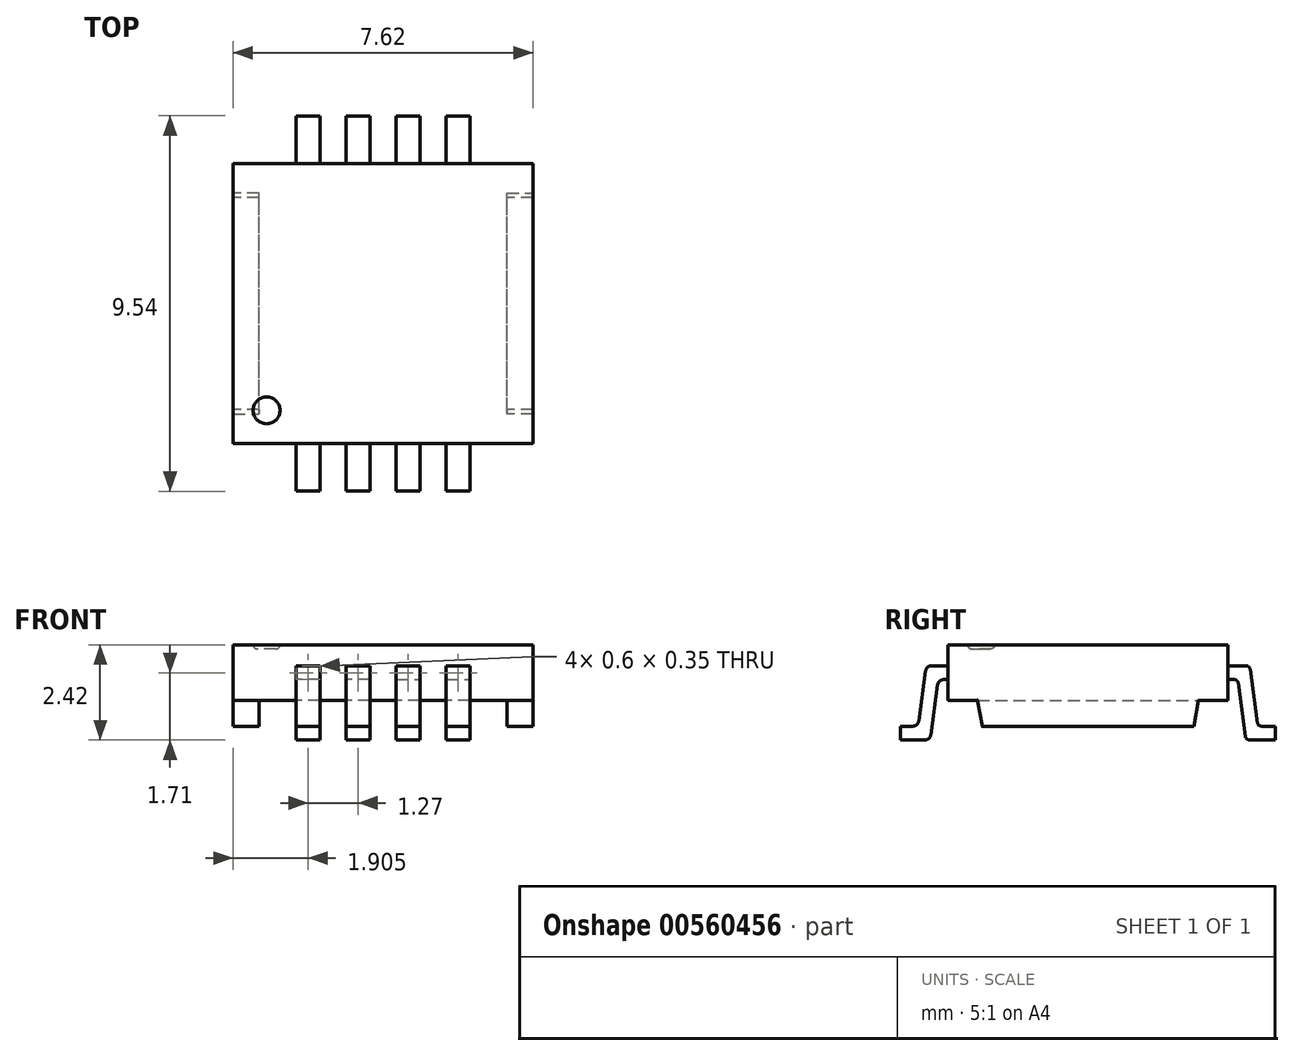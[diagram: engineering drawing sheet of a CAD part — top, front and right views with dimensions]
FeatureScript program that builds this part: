
annotation { "Feature Type Name" : "Feature", "Feature Type Description" : "" }
export const myFeature = defineFeature(function(context is Context, id is Id, definition is map)
    precondition{}
    {
        {
            var Q0;
            Q0=qCreatedBy(makeId("Top.planeOp"),FACE);
            var sketch = newSketch(context, id + "F0", { "sketchPlane" : qUnion([Q0])});
            skLineSegment(sketch, "E0.bottom", {"start": v(3.8, 3.56) * mm, "end": v(-3.81, 3.55) * mm});
            skLineSegment(sketch, "E0.top", {"start": v(3.81, -3.55) * mm, "end": v(-3.8, -3.56) * mm});
            skLineSegment(sketch, "E0.left", {"start": v(3.8, 3.56) * mm, "end": v(3.81, -3.56) * mm});
            skLineSegment(sketch, "E0.right", {"start": v(-3.81, 3.55) * mm, "end": v(-3.8, -3.56) * mm});
            skPoint(sketch, "E0.middle", {"position": v(0, 0) * mm});
            skSolve(sketch);
        }
        {
            var Q0;
            Q0=makeQuery(id+"F0.imprint","IMPRINT",FACE,{"disambiguationData":[TD([[makeQuery(id+"F0.imprint","IMPRINT",EDGE,{"derivedFrom":sQuery(id+"F0.wireOp",EDGE,"E0.bottom")}),1.0]])]});
            var Q1;
            Q1=makeQuery(id+"F0.imprint","IMPRINT",FACE,{"disambiguationData":[TD([[makeQuery(id+"F0.imprint","IMPRINT",EDGE,{"derivedFrom":sQuery(id+"F0.wireOp",EDGE,"f8ecaba3-d954-4120-b82d-af37b7497bcb0.MirrorCS")}),-1.0]])]});
            var Q2;
            Q2=makeQuery(id+"F0.imprint","IMPRINT",FACE,{"disambiguationData":[TD([[makeQuery(id+"F0.imprint","IMPRINT",EDGE,{"derivedFrom":sQuery(id+"F0.wireOp",EDGE,"WD66FqTf-apUJ-U9uG-5Enu-XqBL7MFoTnpj")}),-1.0]])]});
            extrude(context, id + "F1", {"entities" : qUnion([Q0, Q1, Q2]), "endBound" : BoundingType.SYMMETRIC, "depth" : 1.41 * mm, "offsetDistance" : 25 * mm});
        }
        {
            var Q0;
            Q0=makeQuery(id+"F1.opExtrude","CAP_FACE",FACE,{"disambiguationData":[OSD([sQuery(id+"F0.wireOp",EDGE,"E0.bottom"),sQuery(id+"F0.wireOp",EDGE,"E0.top"),sQuery(id+"F0.wireOp",EDGE,"E0.left"),sQuery(id+"F0.wireOp",EDGE,"E0.right")])],"isStart":true});
            var sketch = newSketch(context, id + "F2", { "sketchPlane" : qUnion([Q0])});
            skLineSegment(sketch, "E1", {"start": v(-3.8, 0) * mm, "end": v(-3.8, 2.81) * mm});
            skLineSegment(sketch, "E2", {"start": v(-3.8, 2.81) * mm, "end": v(-3.15, 2.81) * mm});
            skLineSegment(sketch, "E3", {"start": v(-3.15, 2.81) * mm, "end": v(-3.15, -2.81) * mm});
            skLineSegment(sketch, "E4", {"start": v(-3.15, -2.81) * mm, "end": v(-3.81, -2.81) * mm});
            skLineSegment(sketch, "E5", {"start": v(-3.8, -2.81) * mm, "end": v(-3.8, 0) * mm});
            skLineSegment(sketch, "E6.MirrorCS", {"start": v(3.8, 2.81) * mm, "end": v(3.15, 2.81) * mm});
            skLineSegment(sketch, "E7.MirrorCS", {"start": v(3.15, 2.81) * mm, "end": v(3.15, -2.81) * mm});
            skLineSegment(sketch, "E8.MirrorCS", {"start": v(3.8, 0) * mm, "end": v(3.8, 2.81) * mm});
            skLineSegment(sketch, "E9.MirrorCS", {"start": v(3.8, -2.81) * mm, "end": v(3.8, 0) * mm});
            skLineSegment(sketch, "E10.MirrorCS", {"start": v(3.15, -2.81) * mm, "end": v(3.81, -2.81) * mm});
            skSolve(sketch);
        }
        {
            var Q0;
            Q0=makeQuery(id+"F2.imprint","IMPRINT",FACE,{"disambiguationData":[TD([[makeQuery(id+"F2.imprint","IMPRINT",EDGE,{"derivedFrom":sQuery(id+"F2.wireOp",EDGE,"E1")}),-1.0]])]});
            var Q1;
            Q1=makeQuery(id+"F2.imprint","IMPRINT",FACE,{"disambiguationData":[TD([[makeQuery(id+"F2.imprint","IMPRINT",EDGE,{"derivedFrom":sQuery(id+"F2.wireOp",EDGE,"E6.MirrorCS")}),1.0]])]});
            extrude(context, id + "F3", {"entities" : qUnion([Q0, Q1]), "operationType" : NewBodyOperationType.ADD, "depth" : 0.66 * mm, "offsetDistance" : 25 * mm});
        }
        {
            var Q0;
            Q0=makeQuery(id+"F3.boolean.opBoolean","MERGE",FACE,{"derivedFrom":[makeQuery(id+"F1.opExtrude","SWEPT_FACE",FACE,{"disambiguationData":[OSD([sQuery(id+"F0.wireOp",EDGE,"E0.right")])]}),makeQuery(id+"F3.opExtrude","SWEPT_FACE",FACE,{"disambiguationData":[OSD([sQuery(id+"F2.wireOp",EDGE,"E1"),sQuery(id+"F2.wireOp",EDGE,"E5")])]})]});
            var sketch = newSketch(context, id + "F4", { "sketchPlane" : qUnion([Q0])});
            skLineSegment(sketch, "E11", {"start": v(2.8, -0.7) * mm, "end": v(2.69, -1.36) * mm});
            skLineSegment(sketch, "E12", {"start": v(2.69, -1.36) * mm, "end": v(2.8, -1.36) * mm});
            skLineSegment(sketch, "E13", {"start": v(2.8, -1.36) * mm, "end": v(2.8, -0.7) * mm});
            skLineSegment(sketch, "E14.MirrorCS", {"start": v(-2.81, -0.7) * mm, "end": v(-2.69, -1.36) * mm});
            skLineSegment(sketch, "E15.MirrorCS", {"start": v(-2.69, -1.36) * mm, "end": v(-2.81, -1.36) * mm});
            skLineSegment(sketch, "E16.MirrorCS", {"start": v(-2.81, -1.36) * mm, "end": v(-2.81, -0.7) * mm});
            skSolve(sketch);
        }
        {
            var Q0;
            Q0=makeQuery(id+"F4.imprint","IMPRINT",FACE,{"disambiguationData":[TD([[makeQuery(id+"F4.imprint","IMPRINT",EDGE,{"derivedFrom":sQuery(id+"F4.wireOp",EDGE,"E14.MirrorCS")}),-1.0]])]});
            var Q1;
            Q1=makeQuery(id+"F4.imprint","IMPRINT",FACE,{"disambiguationData":[TD([[makeQuery(id+"F4.imprint","IMPRINT",EDGE,{"derivedFrom":sQuery(id+"F4.wireOp",EDGE,"E11")}),1.0]])]});
            extrude(context, id + "F5", {"entities" : qUnion([Q0, Q1]), "operationType" : NewBodyOperationType.REMOVE, "oppositeDirection" : true, "depth" : 25 * mm, "offsetDistance" : 25 * mm});
        }
        {
            var Q0;
            Q0=makeQuery(id+"F1.opExtrude","CAP_EDGE",EDGE,{"disambiguationData":[OSD([sQuery(id+"F0.wireOp",EDGE,"E0.right")])],"isStart":false});
            var Q1;
            Q1=makeQuery(id+"F1.opExtrude","SWEPT_EDGE",EDGE,{"disambiguationData":[OSD([sQuery(id+"F0.wireOp",EDGE,"E0.top"),sQuery(id+"F0.wireOp",EDGE,"E0.right")])]});
            var Q2;
            Q2=makeQuery(id+"F1.opExtrude","CAP_EDGE",EDGE,{"disambiguationData":[OSD([sQuery(id+"F0.wireOp",EDGE,"E0.top")])],"isStart":false});
            var Q3;
            Q3=makeQuery(id+"F1.opExtrude","SWEPT_EDGE",EDGE,{"disambiguationData":[OSD([sQuery(id+"F0.wireOp",EDGE,"E0.bottom"),sQuery(id+"F0.wireOp",EDGE,"E0.right")])]});
            var Q4;
            Q4=makeQuery(id+"F1.opExtrude","SWEPT_EDGE",EDGE,{"disambiguationData":[OSD([sQuery(id+"F0.wireOp",EDGE,"E0.top"),sQuery(id+"F0.wireOp",EDGE,"E0.left")])]});
            var Q5;
            Q5=makeQuery(id+"F1.opExtrude","CAP_EDGE",EDGE,{"disambiguationData":[OSD([sQuery(id+"F0.wireOp",EDGE,"E0.left")])],"isStart":false});
            var Q6;
            Q6=makeQuery(id+"F1.opExtrude","SWEPT_EDGE",EDGE,{"disambiguationData":[OSD([sQuery(id+"F0.wireOp",EDGE,"E0.bottom"),sQuery(id+"F0.wireOp",EDGE,"E0.left")])]});
            var Q7;
            Q7=makeQuery(id+"F1.opExtrude","CAP_EDGE",EDGE,{"disambiguationData":[OSD([sQuery(id+"F0.wireOp",EDGE,"E0.bottom")])],"isStart":false});
            var Q8;
            Q8=makeQuery(id+"F1.opExtrude","CAP_EDGE",EDGE,{"disambiguationData":[OSD([sQuery(id+"F0.wireOp",EDGE,"E0.bottom")])],"isStart":true});
            var Q9;
            Q9=makeQuery(id+"F1.opExtrude","CAP_EDGE",EDGE,{"disambiguationData":[OSD([sQuery(id+"F0.wireOp",EDGE,"E0.top")])],"isStart":true});
            var Q10;
            {var subQ0=sQuery(id+"F0.wireOp",EDGE,"E0.left");var subQ1=sQuery(id+"F0.wireOp",EDGE,"E0.top");Q10=makeQuery(id+"F3.boolean.opBoolean","SPLIT",EDGE,{"disambiguationData":[TD([makeQuery(id+"F1.opExtrude","SWEPT_FACE",FACE,{"disambiguationData":[OSD([subQ1])]})])],"derivedFrom":makeQuery(id+"F1.opExtrude","CAP_EDGE",EDGE,{"disambiguationData":[OSD([subQ0])],"isStart":true})});}
            var Q11;
            Q11=makeQuery(id+"F5.boolean.opBoolean","INTERSECT",EDGE,{"derivedFrom":[makeQuery(id+"F3.boolean.opBoolean","MERGE",FACE,{"derivedFrom":[makeQuery(id+"F1.opExtrude","SWEPT_FACE",FACE,{"disambiguationData":[OSD([sQuery(id+"F0.wireOp",EDGE,"E0.left")])]}),makeQuery(id+"F3.opExtrude","SWEPT_FACE",FACE,{"disambiguationData":[OSD([sQuery(id+"F2.wireOp",EDGE,"E8.MirrorCS"),sQuery(id+"F2.wireOp",EDGE,"E9.MirrorCS")])]})]}),makeQuery(id+"F5.opExtrude","SWEPT_FACE",FACE,{"disambiguationData":[OSD([sQuery(id+"F4.wireOp",EDGE,"E11")])]})]});
            var Q12;
            Q12=makeQuery(id+"F5.boolean.opBoolean","INTERSECT",EDGE,{"derivedFrom":[makeQuery(id+"F3.boolean.opBoolean","MERGE",FACE,{"derivedFrom":[makeQuery(id+"F1.opExtrude","SWEPT_FACE",FACE,{"disambiguationData":[OSD([sQuery(id+"F0.wireOp",EDGE,"E0.left")])]}),makeQuery(id+"F3.opExtrude","SWEPT_FACE",FACE,{"disambiguationData":[OSD([sQuery(id+"F2.wireOp",EDGE,"E8.MirrorCS"),sQuery(id+"F2.wireOp",EDGE,"E9.MirrorCS")])]})]}),makeQuery(id+"F5.opExtrude","SWEPT_FACE",FACE,{"disambiguationData":[OSD([sQuery(id+"F4.wireOp",EDGE,"E14.MirrorCS")])]})]});
            var Q13;
            {var subQ0=sQuery(id+"F0.wireOp",EDGE,"E0.bottom");var subQ1=sQuery(id+"F0.wireOp",EDGE,"E0.left");Q13=makeQuery(id+"F3.boolean.opBoolean","SPLIT",EDGE,{"disambiguationData":[TD([makeQuery(id+"F1.opExtrude","SWEPT_FACE",FACE,{"disambiguationData":[OSD([subQ0])]})])],"derivedFrom":makeQuery(id+"F1.opExtrude","CAP_EDGE",EDGE,{"disambiguationData":[OSD([subQ1])],"isStart":true})});}
            var Q14;
            Q14=makeQuery(id+"F5.boolean.opBoolean","COPY",EDGE,{"derivedFrom":makeQuery(id+"F5.opExtrude","CAP_EDGE",EDGE,{"disambiguationData":[OSD([sQuery(id+"F4.wireOp",EDGE,"E11")])],"isStart":true})});
            var Q15;
            {var subQ0=sQuery(id+"F0.wireOp",EDGE,"E0.top");var subQ1=sQuery(id+"F0.wireOp",EDGE,"E0.right");Q15=makeQuery(id+"F3.boolean.opBoolean","SPLIT",EDGE,{"disambiguationData":[TD([makeQuery(id+"F1.opExtrude","SWEPT_FACE",FACE,{"disambiguationData":[OSD([subQ0])]})])],"derivedFrom":makeQuery(id+"F1.opExtrude","CAP_EDGE",EDGE,{"disambiguationData":[OSD([subQ1])],"isStart":true})});}
            var Q16;
            {var subQ0=sQuery(id+"F0.wireOp",EDGE,"E0.right");var subQ1=sQuery(id+"F0.wireOp",EDGE,"E0.bottom");Q16=makeQuery(id+"F3.boolean.opBoolean","SPLIT",EDGE,{"disambiguationData":[TD([makeQuery(id+"F1.opExtrude","SWEPT_FACE",FACE,{"disambiguationData":[OSD([subQ1])]})])],"derivedFrom":makeQuery(id+"F1.opExtrude","CAP_EDGE",EDGE,{"disambiguationData":[OSD([subQ0])],"isStart":true})});}
            var Q17;
            Q17=makeQuery(id+"F5.boolean.opBoolean","COPY",EDGE,{"derivedFrom":makeQuery(id+"F5.opExtrude","CAP_EDGE",EDGE,{"disambiguationData":[OSD([sQuery(id+"F4.wireOp",EDGE,"E14.MirrorCS")])],"isStart":true})});
            fillet(context, id + "F6", {"entities" : qUnion([Q0, Q1, Q2, Q3, Q4, Q5, Q6, Q7, Q8, Q9, Q10, Q11, Q12, Q13, Q14, Q15, Q16, Q17]), "radius" : 0.01 * mm, "tangentPropagation" : true, "allowEdgeOverflow" : false});
        }
        {
            var Q0;
            Q0=makeQuery(id+"F1.opExtrude","CAP_FACE",FACE,{"disambiguationData":[OSD([sQuery(id+"F0.wireOp",EDGE,"E0.bottom"),sQuery(id+"F0.wireOp",EDGE,"E0.top"),sQuery(id+"F0.wireOp",EDGE,"E0.left"),sQuery(id+"F0.wireOp",EDGE,"E0.right")])],"isStart":false});
            var sketch = newSketch(context, id + "F7", { "sketchPlane" : qUnion([Q0])});
            skCircle(sketch, "E17", {"center": v(-2.96, -2.71) * mm, "radius": 0.34 * mm});
            skSolve(sketch);
        }
        {
            var Q0;
            Q0=makeQuery(id+"F7.imprint","IMPRINT",FACE,{"disambiguationData":[TD([[makeQuery(id+"F7.imprint","IMPRINT",EDGE,{"derivedFrom":sQuery(id+"F7.wireOp",EDGE,"E17")}),1.0]])]});
            extrude(context, id + "F8", {"entities" : qUnion([Q0]), "operationType" : NewBodyOperationType.REMOVE, "oppositeDirection" : true, "depth" : 0.1 * mm, "offsetDistance" : 25 * mm});
        }
        {
            var Q0;
            Q0=makeQuery(id+"F8.boolean.opBoolean","COPY",EDGE,{"derivedFrom":makeQuery(id+"F8.opExtrude","CAP_EDGE",EDGE,{"disambiguationData":[OSD([sQuery(id+"F7.wireOp",EDGE,"E17")])],"isStart":false})});
            fillet(context, id + "F9", {"entities" : qUnion([Q0]), "radius" : 0.1 * mm, "tangentPropagation" : true, "allowEdgeOverflow" : false});
        }
        {
            var Q0;
            Q0=qCreatedBy(makeId("Right.planeOp"),FACE);
            var sketch = newSketch(context, id + "F10", { "sketchPlane" : qUnion([Q0])});
            skLineSegment(sketch, "E18", {"start": v(3.56, 0) * mm, "end": v(3.96, 0) * mm});
            skLineSegment(sketch, "E19", {"start": v(3.96, 0) * mm, "end": v(4.17, -1.53) * mm});
            skLineSegment(sketch, "E20", {"start": v(4.17, -1.53) * mm, "end": v(4.77, -1.53) * mm});
            skLineSegment(sketch, "E21.MirrorCS", {"start": v(-3.56, 0) * mm, "end": v(-3.96, 0) * mm});
            skLineSegment(sketch, "E22.MirrorCS", {"start": v(-3.96, 0) * mm, "end": v(-4.17, -1.53) * mm});
            skLineSegment(sketch, "E23.MirrorCS", {"start": v(-4.17, -1.53) * mm, "end": v(-4.77, -1.53) * mm});
            skSolve(sketch);
        }
        {
            var Q0;
            Q0=makeQuery(id+"F1.opExtrude","SWEPT_FACE",FACE,{"disambiguationData":[OSD([sQuery(id+"F0.wireOp",EDGE,"E0.bottom")])]});
            var sketch = newSketch(context, id + "F11", { "sketchPlane" : qUnion([Q0])});
            skLineSegment(sketch, "E24.bottom", {"start": v(-0.34, -0.17) * mm, "end": v(-0.94, -0.17) * mm});
            skLineSegment(sketch, "E24.top", {"start": v(-0.34, 0.18) * mm, "end": v(-0.94, 0.18) * mm});
            skLineSegment(sketch, "E24.left", {"start": v(-0.34, -0.17) * mm, "end": v(-0.34, 0.18) * mm});
            skLineSegment(sketch, "E24.right", {"start": v(-0.94, -0.18) * mm, "end": v(-0.94, 0.17) * mm});
            skPoint(sketch, "E24.middle", {"position": v(-0.64, 0) * mm});
            skLineSegment(sketch, "E25.bottom", {"start": v(0.33, -0.17) * mm, "end": v(0.93, -0.17) * mm});
            skLineSegment(sketch, "E25.top", {"start": v(0.33, 0.17) * mm, "end": v(0.93, 0.17) * mm});
            skLineSegment(sketch, "E25.left", {"start": v(0.33, -0.17) * mm, "end": v(0.33, 0.18) * mm});
            skLineSegment(sketch, "E25.right", {"start": v(0.93, -0.17) * mm, "end": v(0.93, 0.18) * mm});
            skPoint(sketch, "E25.middle", {"position": v(0.63, 0) * mm});
            skLineSegment(sketch, "E26.bottom", {"start": v(1.6, 0.17) * mm, "end": v(2.2, 0.17) * mm});
            skLineSegment(sketch, "E26.top", {"start": v(1.6, -0.17) * mm, "end": v(2.2, -0.17) * mm});
            skLineSegment(sketch, "E26.left", {"start": v(1.6, 0.17) * mm, "end": v(1.6, -0.17) * mm});
            skLineSegment(sketch, "E26.right", {"start": v(2.2, 0.17) * mm, "end": v(2.2, -0.17) * mm});
            skPoint(sketch, "E26.middle", {"position": v(1.9, 0) * mm});
            skLineSegment(sketch, "E27.MirrorCS", {"start": v(-1.6, 0.17) * mm, "end": v(-1.6, -0.17) * mm});
            skLineSegment(sketch, "E28.MirrorCS", {"start": v(-1.6, 0.17) * mm, "end": v(-2.2, 0.17) * mm});
            skLineSegment(sketch, "E29.MirrorCS", {"start": v(-2.2, 0.17) * mm, "end": v(-2.2, -0.17) * mm});
            skLineSegment(sketch, "E30.MirrorCS", {"start": v(-1.6, -0.17) * mm, "end": v(-2.2, -0.17) * mm});
            skSolve(sketch);
        }
        {
            var Q0;
            Q0=makeQuery(id+"F11.imprint","IMPRINT",FACE,{"disambiguationData":[TD([[makeQuery(id+"F11.imprint","IMPRINT",EDGE,{"derivedFrom":sQuery(id+"F11.wireOp",EDGE,"E27.MirrorCS")}),-1.0]])]});
            var Q1;
            Q1=makeQuery(id+"F11.imprint","IMPRINT",FACE,{"disambiguationData":[TD([[makeQuery(id+"F11.imprint","IMPRINT",EDGE,{"derivedFrom":sQuery(id+"F11.wireOp",EDGE,"E24.bottom")}),-1.0]])]});
            var Q2;
            Q2=makeQuery(id+"F11.imprint","IMPRINT",FACE,{"disambiguationData":[TD([[makeQuery(id+"F11.imprint","IMPRINT",EDGE,{"derivedFrom":sQuery(id+"F11.wireOp",EDGE,"E25.bottom")}),1.0]])]});
            var Q3;
            Q3=makeQuery(id+"F11.imprint","IMPRINT",FACE,{"disambiguationData":[TD([[makeQuery(id+"F11.imprint","IMPRINT",EDGE,{"derivedFrom":sQuery(id+"F11.wireOp",EDGE,"E26.bottom")}),-1.0]])]});
            var Q4;
            Q4=sQuery(id+"F10.wireOp",EDGE,"E18");
            var Q5;
            Q5=sQuery(id+"F10.wireOp",EDGE,"E19");
            var Q6;
            Q6=sQuery(id+"F10.wireOp",EDGE,"E20");
            sweep(context, id + "F12", {"operationType" : NewBodyOperationType.ADD, "profiles" : qUnion([Q0, Q1, Q2, Q3]), "path" : qUnion([Q4, Q5, Q6])});
        }
        {
            var Q0;
            Q0=makeQuery(id+"F12.opSweep","MID_CAP_EDGE",EDGE,{"disambiguationData":[OSD([sQuery(id+"F10.wireOp",VERTEX,"E19.start"),sQuery(id+"F11.wireOp",EDGE,"E26.bottom")])],"capPos":1.0});
            var Q1;
            Q1=makeQuery(id+"F12.opSweep","MID_CAP_EDGE",EDGE,{"disambiguationData":[OSD([sQuery(id+"F10.wireOp",VERTEX,"E20.start"),sQuery(id+"F11.wireOp",EDGE,"E26.bottom")])],"capPos":2.0});
            var Q2;
            Q2=makeQuery(id+"F12.opSweep","MID_CAP_EDGE",EDGE,{"disambiguationData":[OSD([sQuery(id+"F10.wireOp",VERTEX,"E19.start"),sQuery(id+"F11.wireOp",EDGE,"E25.top")])],"capPos":1.0});
            var Q3;
            Q3=makeQuery(id+"F12.opSweep","MID_CAP_EDGE",EDGE,{"disambiguationData":[OSD([sQuery(id+"F10.wireOp",VERTEX,"E20.start"),sQuery(id+"F11.wireOp",EDGE,"E25.top")])],"capPos":2.0});
            var Q4;
            Q4=makeQuery(id+"F12.opSweep","MID_CAP_EDGE",EDGE,{"disambiguationData":[OSD([sQuery(id+"F10.wireOp",VERTEX,"E19.start"),sQuery(id+"F11.wireOp",EDGE,"E24.top")])],"capPos":1.0});
            var Q5;
            Q5=makeQuery(id+"F12.opSweep","MID_CAP_EDGE",EDGE,{"disambiguationData":[OSD([sQuery(id+"F10.wireOp",VERTEX,"E20.start"),sQuery(id+"F11.wireOp",EDGE,"E24.top")])],"capPos":2.0});
            var Q6;
            Q6=makeQuery(id+"F12.opSweep","MID_CAP_EDGE",EDGE,{"disambiguationData":[OSD([sQuery(id+"F10.wireOp",VERTEX,"E19.start"),sQuery(id+"F11.wireOp",EDGE,"E28.MirrorCS")])],"capPos":1.0});
            var Q7;
            Q7=makeQuery(id+"F12.opSweep","MID_CAP_EDGE",EDGE,{"disambiguationData":[OSD([sQuery(id+"F10.wireOp",VERTEX,"E20.start"),sQuery(id+"F11.wireOp",EDGE,"E28.MirrorCS")])],"capPos":2.0});
            var Q8;
            Q8=makeQuery(id+"F12.opSweep","MID_CAP_EDGE",EDGE,{"disambiguationData":[OSD([sQuery(id+"F10.wireOp",VERTEX,"E19.start"),sQuery(id+"F11.wireOp",EDGE,"E30.MirrorCS")])],"capPos":1.0});
            var Q9;
            Q9=makeQuery(id+"F12.opSweep","MID_CAP_EDGE",EDGE,{"disambiguationData":[OSD([sQuery(id+"F10.wireOp",VERTEX,"E19.start"),sQuery(id+"F11.wireOp",EDGE,"E24.bottom")])],"capPos":1.0});
            var Q10;
            Q10=makeQuery(id+"F12.opSweep","MID_CAP_EDGE",EDGE,{"disambiguationData":[OSD([sQuery(id+"F10.wireOp",VERTEX,"E19.start"),sQuery(id+"F11.wireOp",EDGE,"E25.bottom")])],"capPos":1.0});
            var Q11;
            Q11=makeQuery(id+"F12.opSweep","MID_CAP_EDGE",EDGE,{"disambiguationData":[OSD([sQuery(id+"F10.wireOp",VERTEX,"E19.start"),sQuery(id+"F11.wireOp",EDGE,"E26.top")])],"capPos":1.0});
            var Q12;
            Q12=makeQuery(id+"F12.opSweep","MID_CAP_EDGE",EDGE,{"disambiguationData":[OSD([sQuery(id+"F10.wireOp",VERTEX,"E20.start"),sQuery(id+"F11.wireOp",EDGE,"E26.top")])],"capPos":2.0});
            var Q13;
            Q13=makeQuery(id+"F12.opSweep","MID_CAP_EDGE",EDGE,{"disambiguationData":[OSD([sQuery(id+"F10.wireOp",VERTEX,"E20.start"),sQuery(id+"F11.wireOp",EDGE,"E25.bottom")])],"capPos":2.0});
            var Q14;
            Q14=makeQuery(id+"F12.opSweep","MID_CAP_EDGE",EDGE,{"disambiguationData":[OSD([sQuery(id+"F10.wireOp",VERTEX,"E20.start"),sQuery(id+"F11.wireOp",EDGE,"E24.bottom")])],"capPos":2.0});
            var Q15;
            Q15=makeQuery(id+"F12.opSweep","MID_CAP_EDGE",EDGE,{"disambiguationData":[OSD([sQuery(id+"F10.wireOp",VERTEX,"E20.start"),sQuery(id+"F11.wireOp",EDGE,"E30.MirrorCS")])],"capPos":2.0});
            fillet(context, id + "F13", {"entities" : qUnion([Q0, Q1, Q2, Q3, Q4, Q5, Q6, Q7, Q8, Q9, Q10, Q11, Q12, Q13, Q14, Q15]), "radius" : 0.1 * mm, "tangentPropagation" : true, "allowEdgeOverflow" : false});
        }
        {
            var Q0;
            Q0=makeQuery(id+"F1.opExtrude","SWEPT_FACE",FACE,{"disambiguationData":[OSD([sQuery(id+"F0.wireOp",EDGE,"E0.top")])]});
            var sketch = newSketch(context, id + "F14", { "sketchPlane" : qUnion([Q0])});
            skLineSegment(sketch, "E31.bottom", {"start": v(-1.6, 0.18) * mm, "end": v(-2.2, 0.18) * mm});
            skLineSegment(sketch, "E31.top", {"start": v(-1.6, -0.18) * mm, "end": v(-2.2, -0.18) * mm});
            skLineSegment(sketch, "E31.left", {"start": v(-1.6, 0.18) * mm, "end": v(-1.6, -0.18) * mm});
            skLineSegment(sketch, "E31.right", {"start": v(-2.2, 0.18) * mm, "end": v(-2.2, -0.18) * mm});
            skPoint(sketch, "E31.middle", {"position": v(-1.9, 0) * mm});
            skLineSegment(sketch, "E32.bottom", {"start": v(-0.34, 0.18) * mm, "end": v(-0.94, 0.18) * mm});
            skLineSegment(sketch, "E32.top", {"start": v(-0.34, -0.18) * mm, "end": v(-0.94, -0.18) * mm});
            skLineSegment(sketch, "E32.left", {"start": v(-0.34, 0.18) * mm, "end": v(-0.34, -0.18) * mm});
            skLineSegment(sketch, "E32.right", {"start": v(-0.94, 0.18) * mm, "end": v(-0.94, -0.18) * mm});
            skPoint(sketch, "E32.middle", {"position": v(-0.64, 0) * mm});
            skLineSegment(sketch, "E33.MirrorCS", {"start": v(0.33, 0.18) * mm, "end": v(0.33, -0.18) * mm});
            skLineSegment(sketch, "E34.MirrorCS", {"start": v(0.33, 0.18) * mm, "end": v(0.93, 0.18) * mm});
            skLineSegment(sketch, "E35.MirrorCS", {"start": v(0.33, -0.18) * mm, "end": v(0.93, -0.18) * mm});
            skLineSegment(sketch, "E36.MirrorCS", {"start": v(0.93, 0.18) * mm, "end": v(0.93, -0.18) * mm});
            skLineSegment(sketch, "E37.MirrorCS", {"start": v(1.6, 0.18) * mm, "end": v(1.6, -0.18) * mm});
            skLineSegment(sketch, "E38.MirrorCS", {"start": v(1.6, 0.18) * mm, "end": v(2.2, 0.18) * mm});
            skLineSegment(sketch, "E39.MirrorCS", {"start": v(2.2, 0.18) * mm, "end": v(2.2, -0.18) * mm});
            skLineSegment(sketch, "E40.MirrorCS", {"start": v(1.6, -0.18) * mm, "end": v(2.2, -0.18) * mm});
            skSolve(sketch);
        }
        {
            var Q0;
            Q0=makeQuery(id+"F14.imprint","IMPRINT",FACE,{"disambiguationData":[TD([[makeQuery(id+"F14.imprint","IMPRINT",EDGE,{"derivedFrom":sQuery(id+"F14.wireOp",EDGE,"E31.bottom")}),1.0]])]});
            var Q1;
            Q1=makeQuery(id+"F14.imprint","IMPRINT",FACE,{"disambiguationData":[TD([[makeQuery(id+"F14.imprint","IMPRINT",EDGE,{"derivedFrom":sQuery(id+"F14.wireOp",EDGE,"E32.bottom")}),1.0]])]});
            var Q2;
            Q2=makeQuery(id+"F14.imprint","IMPRINT",FACE,{"disambiguationData":[TD([[makeQuery(id+"F14.imprint","IMPRINT",EDGE,{"derivedFrom":sQuery(id+"F14.wireOp",EDGE,"E33.MirrorCS")}),1.0]])]});
            var Q3;
            Q3=makeQuery(id+"F14.imprint","IMPRINT",FACE,{"disambiguationData":[TD([[makeQuery(id+"F14.imprint","IMPRINT",EDGE,{"derivedFrom":sQuery(id+"F14.wireOp",EDGE,"E37.MirrorCS")}),1.0]])]});
            var Q4;
            Q4=sQuery(id+"F10.wireOp",EDGE,"E21.MirrorCS");
            var Q5;
            Q5=sQuery(id+"F10.wireOp",EDGE,"E22.MirrorCS");
            var Q6;
            Q6=sQuery(id+"F10.wireOp",EDGE,"E23.MirrorCS");
            sweep(context, id + "F15", {"operationType" : NewBodyOperationType.ADD, "profiles" : qUnion([Q0, Q1, Q2, Q3]), "path" : qUnion([Q4, Q5, Q6])});
        }
        {
            var Q0;
            Q0=makeQuery(id+"F15.opSweep","MID_CAP_EDGE",EDGE,{"disambiguationData":[OSD([sQuery(id+"F10.wireOp",VERTEX,"E22.MirrorCS.start"),sQuery(id+"F14.wireOp",EDGE,"E31.bottom")])],"capPos":1.0});
            var Q1;
            Q1=makeQuery(id+"F15.opSweep","MID_CAP_EDGE",EDGE,{"disambiguationData":[OSD([sQuery(id+"F10.wireOp",VERTEX,"E22.MirrorCS.start"),sQuery(id+"F14.wireOp",EDGE,"E32.bottom")])],"capPos":1.0});
            var Q2;
            Q2=makeQuery(id+"F15.opSweep","MID_CAP_EDGE",EDGE,{"disambiguationData":[OSD([sQuery(id+"F10.wireOp",VERTEX,"E22.MirrorCS.start"),sQuery(id+"F14.wireOp",EDGE,"E34.MirrorCS")])],"capPos":1.0});
            var Q3;
            Q3=makeQuery(id+"F15.opSweep","MID_CAP_EDGE",EDGE,{"disambiguationData":[OSD([sQuery(id+"F10.wireOp",VERTEX,"E22.MirrorCS.start"),sQuery(id+"F14.wireOp",EDGE,"E38.MirrorCS")])],"capPos":1.0});
            var Q4;
            Q4=makeQuery(id+"F15.opSweep","MID_CAP_EDGE",EDGE,{"disambiguationData":[OSD([sQuery(id+"F10.wireOp",VERTEX,"E23.MirrorCS.start"),sQuery(id+"F14.wireOp",EDGE,"E31.bottom")])],"capPos":2.0});
            var Q5;
            Q5=makeQuery(id+"F15.opSweep","MID_CAP_EDGE",EDGE,{"disambiguationData":[OSD([sQuery(id+"F10.wireOp",VERTEX,"E23.MirrorCS.start"),sQuery(id+"F14.wireOp",EDGE,"E32.bottom")])],"capPos":2.0});
            var Q6;
            Q6=makeQuery(id+"F15.opSweep","MID_CAP_EDGE",EDGE,{"disambiguationData":[OSD([sQuery(id+"F10.wireOp",VERTEX,"E23.MirrorCS.start"),sQuery(id+"F14.wireOp",EDGE,"E34.MirrorCS")])],"capPos":2.0});
            var Q7;
            Q7=makeQuery(id+"F15.opSweep","MID_CAP_EDGE",EDGE,{"disambiguationData":[OSD([sQuery(id+"F10.wireOp",VERTEX,"E23.MirrorCS.start"),sQuery(id+"F14.wireOp",EDGE,"E38.MirrorCS")])],"capPos":2.0});
            var Q8;
            Q8=makeQuery(id+"F15.opSweep","MID_CAP_EDGE",EDGE,{"disambiguationData":[OSD([sQuery(id+"F10.wireOp",VERTEX,"E22.MirrorCS.start"),sQuery(id+"F14.wireOp",EDGE,"E31.top")])],"capPos":1.0});
            var Q9;
            Q9=makeQuery(id+"F15.opSweep","MID_CAP_EDGE",EDGE,{"disambiguationData":[OSD([sQuery(id+"F10.wireOp",VERTEX,"E22.MirrorCS.start"),sQuery(id+"F14.wireOp",EDGE,"E32.top")])],"capPos":1.0});
            var Q10;
            Q10=makeQuery(id+"F15.opSweep","MID_CAP_EDGE",EDGE,{"disambiguationData":[OSD([sQuery(id+"F10.wireOp",VERTEX,"E22.MirrorCS.start"),sQuery(id+"F14.wireOp",EDGE,"E35.MirrorCS")])],"capPos":1.0});
            var Q11;
            Q11=makeQuery(id+"F15.opSweep","MID_CAP_EDGE",EDGE,{"disambiguationData":[OSD([sQuery(id+"F10.wireOp",VERTEX,"E22.MirrorCS.start"),sQuery(id+"F14.wireOp",EDGE,"E40.MirrorCS")])],"capPos":1.0});
            var Q12;
            Q12=makeQuery(id+"F15.opSweep","MID_CAP_EDGE",EDGE,{"disambiguationData":[OSD([sQuery(id+"F10.wireOp",VERTEX,"E23.MirrorCS.start"),sQuery(id+"F14.wireOp",EDGE,"E35.MirrorCS")])],"capPos":2.0});
            var Q13;
            Q13=makeQuery(id+"F15.opSweep","MID_CAP_EDGE",EDGE,{"disambiguationData":[OSD([sQuery(id+"F10.wireOp",VERTEX,"E23.MirrorCS.start"),sQuery(id+"F14.wireOp",EDGE,"E32.top")])],"capPos":2.0});
            var Q14;
            Q14=makeQuery(id+"F15.opSweep","MID_CAP_EDGE",EDGE,{"disambiguationData":[OSD([sQuery(id+"F10.wireOp",VERTEX,"E23.MirrorCS.start"),sQuery(id+"F14.wireOp",EDGE,"E31.top")])],"capPos":2.0});
            var Q15;
            Q15=makeQuery(id+"F15.opSweep","MID_CAP_EDGE",EDGE,{"disambiguationData":[OSD([sQuery(id+"F10.wireOp",VERTEX,"E23.MirrorCS.start"),sQuery(id+"F14.wireOp",EDGE,"E40.MirrorCS")])],"capPos":2.0});
            fillet(context, id + "F16", {"entities" : qUnion([Q0, Q1, Q2, Q3, Q4, Q5, Q6, Q7, Q8, Q9, Q10, Q11, Q12, Q13, Q14, Q15]), "radius" : 0.15 * mm, "tangentPropagation" : true, "allowEdgeOverflow" : false});
        }
    });
